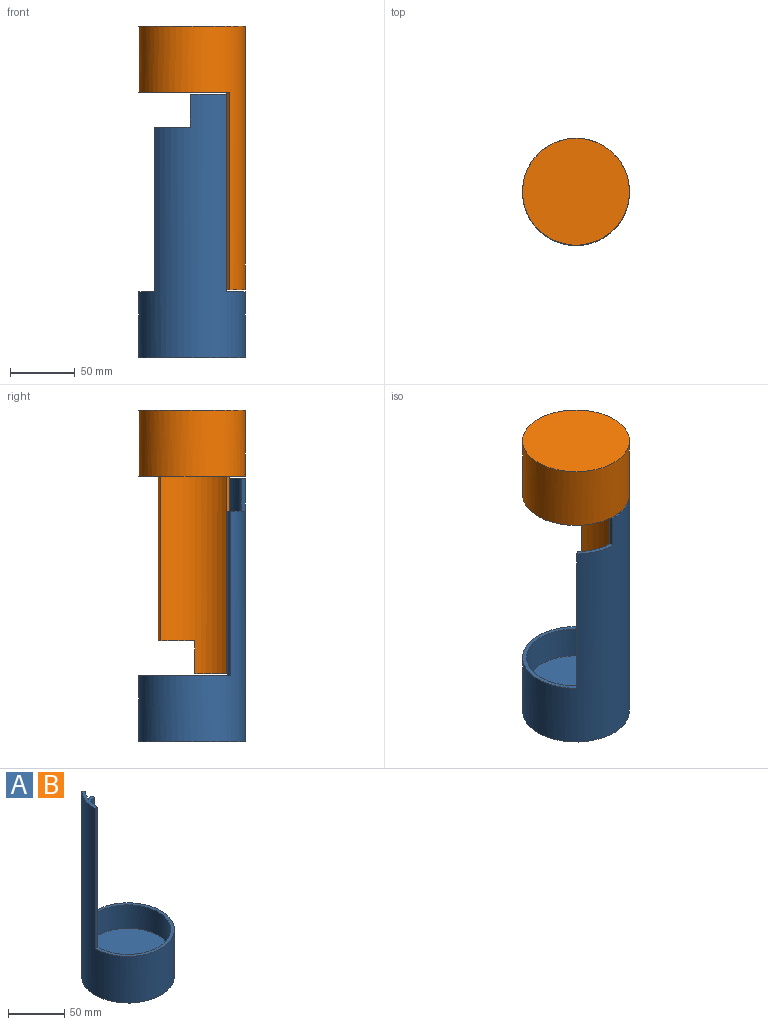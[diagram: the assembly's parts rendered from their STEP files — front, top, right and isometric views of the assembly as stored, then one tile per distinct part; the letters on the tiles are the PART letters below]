
ASSEMBLY  parts=2 mates=1
PART A: 10 faces, bbox 82.6x82.6x203.2 mm
  f0: plane 82.55x82.55mm, normal (0,0,1), area 606.6mm2, adj f2,f3,f5,f6
  f1: plane 76.2x76.2mm, normal (0,0,1), area 4560.4mm2, adj f2
  f2: cylinder r=38.1mm len=177.8mm, axis (0,0,-1), area 13877.4mm2, adj f0,f1,f5,f6,f7,f8,f9
  f3: cylinder r=41.27mm len=203.2mm, axis (0,0,-1), area 21668.2mm2, adj f0,f4,f5,f6,f7,f8,f9
  f4: plane 82.55x82.55mm, normal (0,0,-1), area 5352.1mm2, adj f3
  f5: plane 152.4x3.18mm, normal (0,-1,0), area 483.9mm2, adj f0,f2,f3,f9
  f6: plane 127x3.19mm, normal (1,0,0), area 405.3mm2, adj f0,f2,f3,f7
  f7: plane 26.55x15.6mm, normal (0,0,1), area 92.6mm2, adj f2,f3,f6,f8
  f8: plane 25.4x2.25mm, normal (0.71,0.71,0), area 80.8mm2, adj f2,f3,f7,f9
  f9: plane 27.73x12.95mm, normal (0,0,1), area 92.6mm2, adj f2,f3,f5,f8
PART B: same geometry as A
PLACE A rot(axis=(0,0,1),130.3deg) t=(-154.66,-105.34,-147.85)mm
PLACE B rot(axis=(-0.38,-0.92,0),180deg) t=(-154.66,-105.34,107.73)mm fixed
MATE cylindrical B.f3 <-> A.f3  axis (0,0,1) through (-154.66,-105.34,6.13)mm
